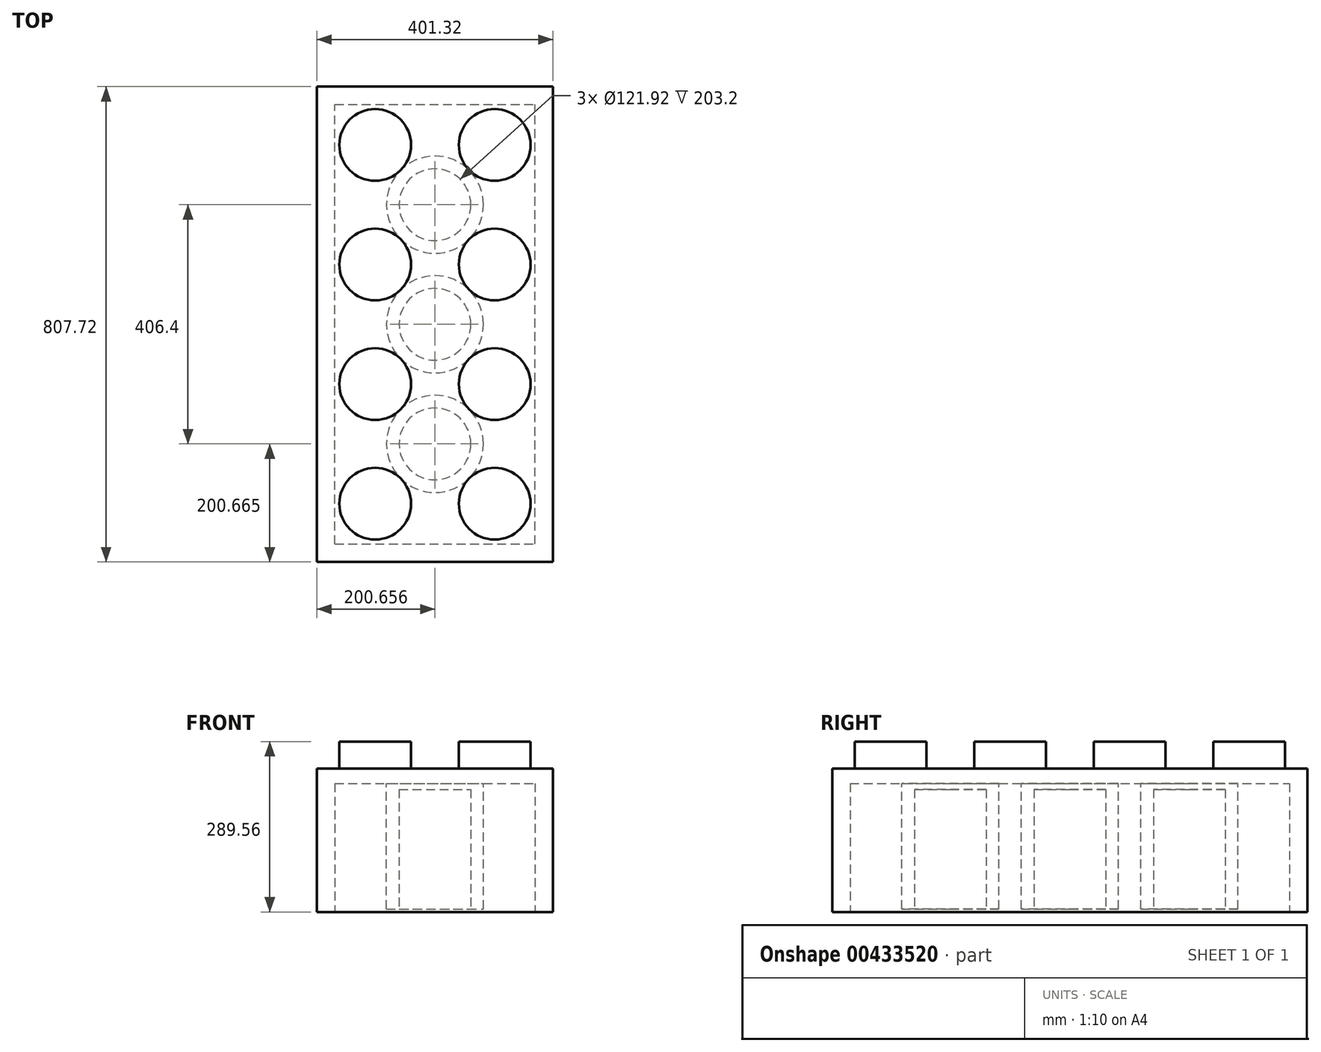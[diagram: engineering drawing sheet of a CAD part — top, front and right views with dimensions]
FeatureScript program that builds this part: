
annotation { "Feature Type Name" : "Feature", "Feature Type Description" : "" }
export const myFeature = defineFeature(function(context is Context, id is Id, definition is map)
    precondition{}
    {
        {
            var Q0;
            Q0=qCreatedBy(makeId("Top.planeOp"),FACE);
            var sketch = newSketch(context, id + "F0", { "sketchPlane" : qUnion([Q0])});
            skLineSegment(sketch, "E0.bottom", {"start": v(-168.28, 778.9) * mm, "end": v(233.04, 778.9) * mm});
            skLineSegment(sketch, "E0.top", {"start": v(-168.28, -28.82) * mm, "end": v(233.04, -28.82) * mm});
            skLineSegment(sketch, "E0.left", {"start": v(-168.28, 778.9) * mm, "end": v(-168.28, -28.82) * mm});
            skLineSegment(sketch, "E0.right", {"start": v(233.04, 778.9) * mm, "end": v(233.04, -28.82) * mm});
            skSolve(sketch);
        }
        {
            var Q0;
            Q0=makeQuery(id+"F0.imprint","IMPRINT",FACE,{"disambiguationData":[TD([[makeQuery(id+"F0.imprint","IMPRINT",EDGE,{"derivedFrom":sQuery(id+"F0.wireOp",EDGE,"E0.bottom")}),-1.0]])]});
            extrude(context, id + "F1", {"entities" : qUnion([Q0]), "depth" : 243.84 * mm});
        }
        {
            var Q0;
            Q0=makeQuery(id+"F1.opExtrude","CAP_FACE",FACE,{"disambiguationData":[OSD([sQuery(id+"F0.wireOp",EDGE,"E0.bottom"),sQuery(id+"F0.wireOp",EDGE,"E0.top"),sQuery(id+"F0.wireOp",EDGE,"E0.left"),sQuery(id+"F0.wireOp",EDGE,"E0.right")])],"isStart":false});
            var sketch = newSketch(context, id + "F2", { "sketchPlane" : qUnion([Q0])});
            skCircle(sketch, "E1", {"center": v(-69.22, 70.24) * mm, "radius": 60.96 * mm});
            skCircle(sketch, "E2.0.1.0", {"center": v(-69.22, 273.44) * mm, "radius": 60.96 * mm});
            skCircle(sketch, "E2.0.2.0", {"center": v(-69.22, 476.64) * mm, "radius": 60.96 * mm});
            skCircle(sketch, "E2.0.3.0", {"center": v(-69.22, 679.84) * mm, "radius": 60.96 * mm});
            skCircle(sketch, "E2.1.0.0", {"center": v(133.98, 70.24) * mm, "radius": 60.96 * mm});
            skCircle(sketch, "E2.1.1.0", {"center": v(133.98, 273.44) * mm, "radius": 60.96 * mm});
            skCircle(sketch, "E2.1.2.0", {"center": v(133.98, 476.64) * mm, "radius": 60.96 * mm});
            skCircle(sketch, "E2.1.3.0", {"center": v(133.98, 679.84) * mm, "radius": 60.96 * mm});
            skLineSegment(sketch, "E2.direction1", {"start": v(-69.22, 70.24) * mm, "end": v(133.98, 70.24) * mm, "construction": true});
            skLineSegment(sketch, "E2.direction2", {"start": v(-69.22, 70.24) * mm, "end": v(-69.22, 273.44) * mm, "construction": true});
            skSolve(sketch);
        }
        {
            var Q0;
            Q0=qSketchRegion(id+"F2",true);
            extrude(context, id + "F3", {"entities" : qUnion([Q0]), "operationType" : NewBodyOperationType.ADD, "depth" : 45.72 * mm});
        }
        {
            var Q0;
            Q0=makeQuery(id+"F1.opExtrude","CAP_FACE",FACE,{"disambiguationData":[OSD([sQuery(id+"F0.wireOp",EDGE,"E0.bottom"),sQuery(id+"F0.wireOp",EDGE,"E0.top"),sQuery(id+"F0.wireOp",EDGE,"E0.left"),sQuery(id+"F0.wireOp",EDGE,"E0.right")])],"isStart":true});
            var sketch = newSketch(context, id + "F4", { "sketchPlane" : qUnion([Q0])});
            skLineSegment(sketch, "E3.bottom", {"start": v(-137.8, -1.66) * mm, "end": v(202.56, -1.66) * mm});
            skLineSegment(sketch, "E3.top", {"start": v(-137.8, -748.42) * mm, "end": v(202.56, -748.42) * mm});
            skLineSegment(sketch, "E3.left", {"start": v(-137.8, -1.66) * mm, "end": v(-137.8, -748.42) * mm});
            skLineSegment(sketch, "E3.right", {"start": v(202.56, -1.66) * mm, "end": v(202.56, -748.42) * mm});
            skSolve(sketch);
        }
        {
            var Q0;
            Q0=qSketchRegion(id+"F4",true);
            extrude(context, id + "F5", {"entities" : qUnion([Q0]), "operationType" : NewBodyOperationType.REMOVE, "oppositeDirection" : true, "depth" : 218.44 * mm});
        }
        {
            var Q0;
            Q0=makeQuery(id+"F5.boolean.opBoolean","COPY",FACE,{"derivedFrom":makeQuery(id+"F5.opExtrude","CAP_FACE",FACE,{"disambiguationData":[OSD([sQuery(id+"F4.wireOp",EDGE,"E3.bottom"),sQuery(id+"F4.wireOp",EDGE,"E3.top"),sQuery(id+"F4.wireOp",EDGE,"E3.left"),sQuery(id+"F4.wireOp",EDGE,"E3.right")])],"isStart":false})});
            var sketch = newSketch(context, id + "F6", { "sketchPlane" : qUnion([Q0])});
            skCircle(sketch, "E4", {"center": v(32.38, -578.24) * mm, "radius": 82.55 * mm});
            skCircle(sketch, "E5.0.1.0", {"center": v(32.38, -375.04) * mm, "radius": 82.55 * mm});
            skCircle(sketch, "E5.0.2.0", {"center": v(32.38, -171.84) * mm, "radius": 82.55 * mm});
            skLineSegment(sketch, "E5.direction1", {"start": v(32.38, -578.24) * mm, "end": v(57.78, -578.24) * mm, "construction": true});
            skLineSegment(sketch, "E5.direction2", {"start": v(32.38, -578.24) * mm, "end": v(32.38, -375.04) * mm, "construction": true});
            skSolve(sketch);
        }
        {
            var Q0;
            Q0=qSketchRegion(id+"F6",true);
            extrude(context, id + "F7", {"entities" : qUnion([Q0]), "operationType" : NewBodyOperationType.ADD, "depth" : 213.36 * mm});
        }
        {
            var Q0;
            Q0=makeQuery(id+"F7.opExtrude","CAP_FACE",FACE,{"disambiguationData":[OSD([sQuery(id+"F6.wireOp",EDGE,"E5.0.2.0")])],"isStart":false});
            var sketch = newSketch(context, id + "F8", { "sketchPlane" : qUnion([Q0])});
            skCircle(sketch, "E6", {"center": v(32.38, -171.84) * mm, "radius": 60.96 * mm});
            skCircle(sketch, "E7.0.1.0", {"center": v(32.38, -375.04) * mm, "radius": 60.96 * mm});
            skCircle(sketch, "E7.0.2.0", {"center": v(32.38, -578.24) * mm, "radius": 60.96 * mm});
            skLineSegment(sketch, "E7.direction1", {"start": v(32.38, -171.84) * mm, "end": v(57.78, -171.84) * mm, "construction": true});
            skLineSegment(sketch, "E7.direction2", {"start": v(32.38, -171.84) * mm, "end": v(32.38, -375.04) * mm, "construction": true});
            skSolve(sketch);
        }
        {
            var Q0;
            Q0=qSketchRegion(id+"F8",true);
            extrude(context, id + "F9", {"entities" : qUnion([Q0]), "operationType" : NewBodyOperationType.REMOVE, "oppositeDirection" : true, "depth" : 203.2 * mm});
        }
    });
